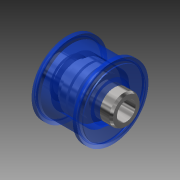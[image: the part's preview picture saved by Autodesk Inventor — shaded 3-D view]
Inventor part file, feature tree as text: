
AUTODESK INVENTOR PART (.ipt)
format: ipt  version: 2014 (Build 180170000, 170)  size: 275,456 bytes
history: native  units: in
note: dims shown in document units (in); Inventor stores cm internally (conversion verified against a paired STEP export)
features: other x2, revolve x2, sketch x1
ambient origin geometry x8: Origin, YZ Plane, XZ Plane, XY Plane, X Axis, Y Axis, Z Axis, Center Point
bodies: Body1 (feature_tree), Body2 (feature_tree)
feature tree (5):
  other  "Solid1 - Hub"
  sketch  "Sketch1"  dims[d0=0.0625in d2=1.88in d3=0.78in d4=1.91in d5=1.31in d6=90.0deg d8=90.0deg d9=0.065in d10=0.13in d11=1.13in d12=0.0625in d13=0.226in d14=0.226in d15=0.226in d17=0.5497in d19=0.5497in d20=0.5497in d21=0.0565in d22=0.1695in d23=0.0864in d24=0.226in d25=0.5497in d26=0.5497in d27=0.226in d28=0.5497in d30=0.113in d31=0.113in d32=0.113in d33=0.3275in d34=0.3275in]
  revolve  "Revolution1 - Hub"  [1 undecoded]
  revolve  "Revolution3"  [1 undecoded]
  other  "Solid2 - Cover"
note: 2 required parameter values undecoded (feature->parameter linkage not recoverable at this tier; creation-order binding heuristic only, values carry confidence <= 0.55)
